# Revit family: Lighting-ArredoUrbano-GEWISS-EXTRO-SNODO
name_source: partatom
category: Apparecchi per illuminazione
units: mm (PartAtom-declared; Revit-internal decimal feet)

## family parameters
Condiviso = No
Host = Superficie
Punto di calcolo locali = Sì
Quota connettore circolare = Usa diametro
Sorgente d'illuminazione = No
Taglio con vuoti quando caricato = No
Tipo di parte = Normale

## types (1)
- GW82290 - SNODO DI ORIENTAMENTO EXTRO G.GRAF.
    Catalogo = LIGHTING
    Codice Electrocod = 240
    Colore = Grigio grafite
    Descrizione = SNODO DI ORIENTAMENTO EXTRO G.GRAF.
    Dim. esterne BxHxP (mm) = 140x120x100
    IDF = 4f176054-faad-4191-99b6-8cab5ac3d145
    IDT = 005f315cd5464f4fa58236bfda421664
    Immagine tipo = GW82290.jpg
    Materiale = Pressofusione di alluminio
    Materiale elemento = Grigio grafite
    Modello = GW82290
    Produttore = GEWISS S.p.A.
    Prospetto di default = 1219 mm
    SEO = Snodo
    Scheda Tecnica = https://www.gewiss.com
    URL = https://www.gewiss.com
    Versione file RFA = 20.11
